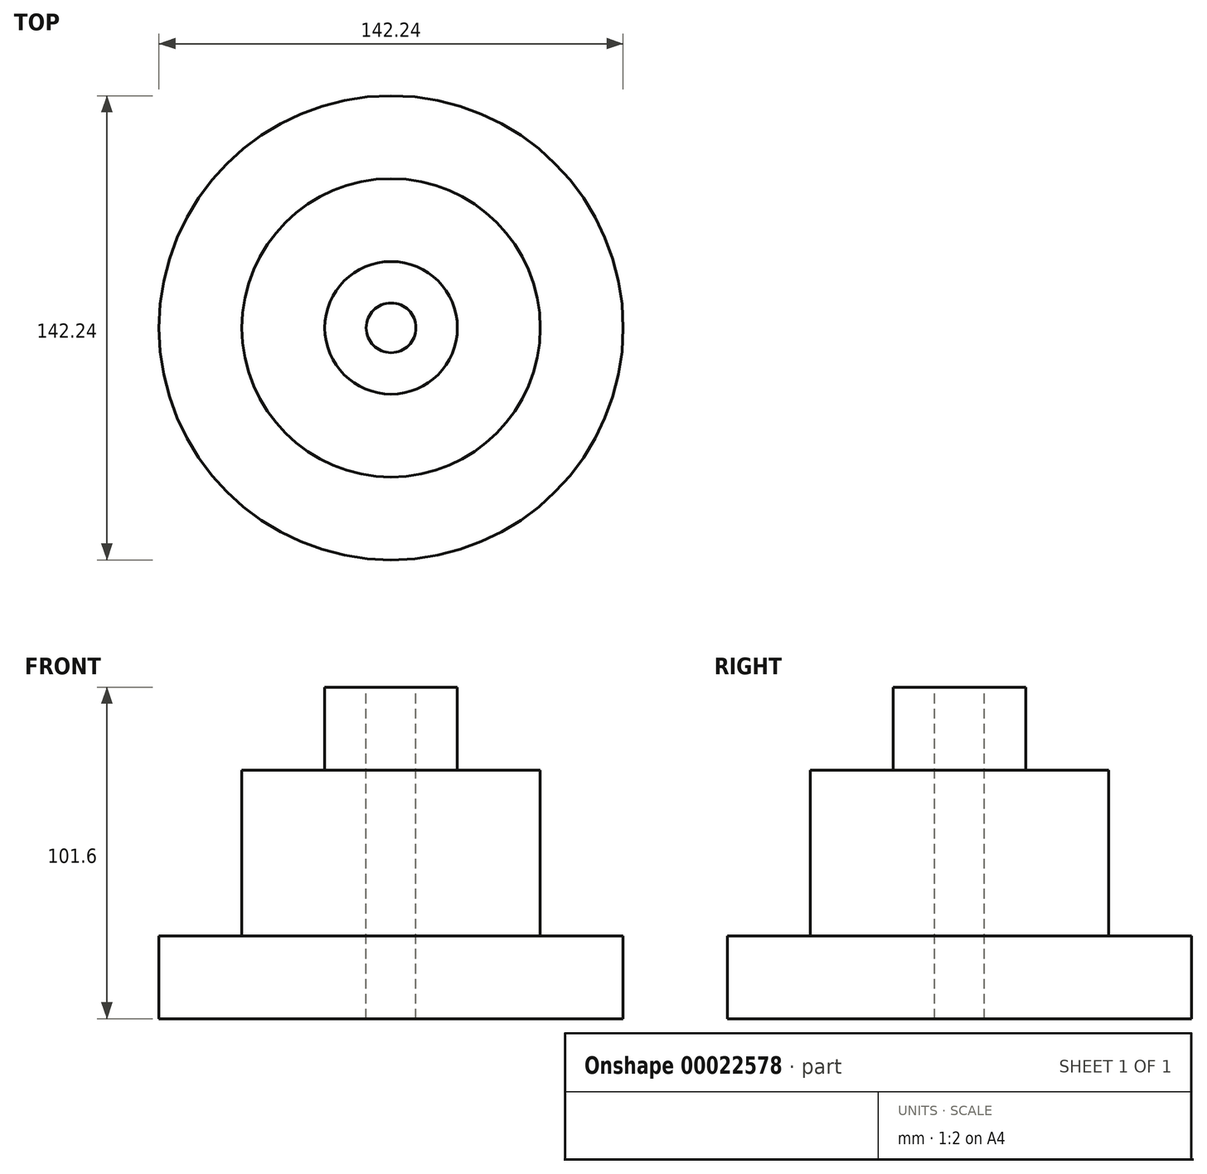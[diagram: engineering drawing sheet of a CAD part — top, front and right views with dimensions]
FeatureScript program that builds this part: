
annotation { "Feature Type Name" : "Feature", "Feature Type Description" : "" }
export const myFeature = defineFeature(function(context is Context, id is Id, definition is map)
    precondition{}
    {
        {
            var Q0;
            Q0=qCreatedBy(makeId("Front.planeOp"),FACE);
            var sketch = newSketch(context, id + "F0", { "sketchPlane" : qUnion([Q0])});
            skLineSegment(sketch, "E0", {"start": v(-9.74, 43.5) * mm, "end": v(-9.74, -57.47) * mm});
            skLineSegment(sketch, "E1", {"start": v(-2.12, 43.5) * mm, "end": v(-2.12, -58.1) * mm});
            skLineSegment(sketch, "E2", {"start": v(-2.12, 43.5) * mm, "end": v(10.58, 43.5) * mm});
            skLineSegment(sketch, "E3", {"start": v(10.58, 43.5) * mm, "end": v(10.58, 18.1) * mm});
            skLineSegment(sketch, "E4", {"start": v(10.58, 18.1) * mm, "end": v(35.98, 18.1) * mm});
            skLineSegment(sketch, "E5", {"start": v(35.98, 18.1) * mm, "end": v(35.98, -32.7) * mm});
            skLineSegment(sketch, "E6", {"start": v(35.98, -32.7) * mm, "end": v(61.38, -32.7) * mm});
            skLineSegment(sketch, "E7", {"start": v(61.38, -32.7) * mm, "end": v(61.38, -58.1) * mm});
            skLineSegment(sketch, "E8", {"start": v(61.38, -58.1) * mm, "end": v(-2.12, -58.1) * mm});
            skSolve(sketch);
        }
        {
            var Q0;
            Q0 = qSketchRegion(id + "F0", true);
            var Q1;
            Q1=sQuery(id+"F0.wireOp",EDGE,"E0");
            revolve(context, id + "F1", {"entities" : qUnion([Q0]), "axis" : qUnion([Q1]), "revolveType" : RevolveType.FULL});
        }
    });
